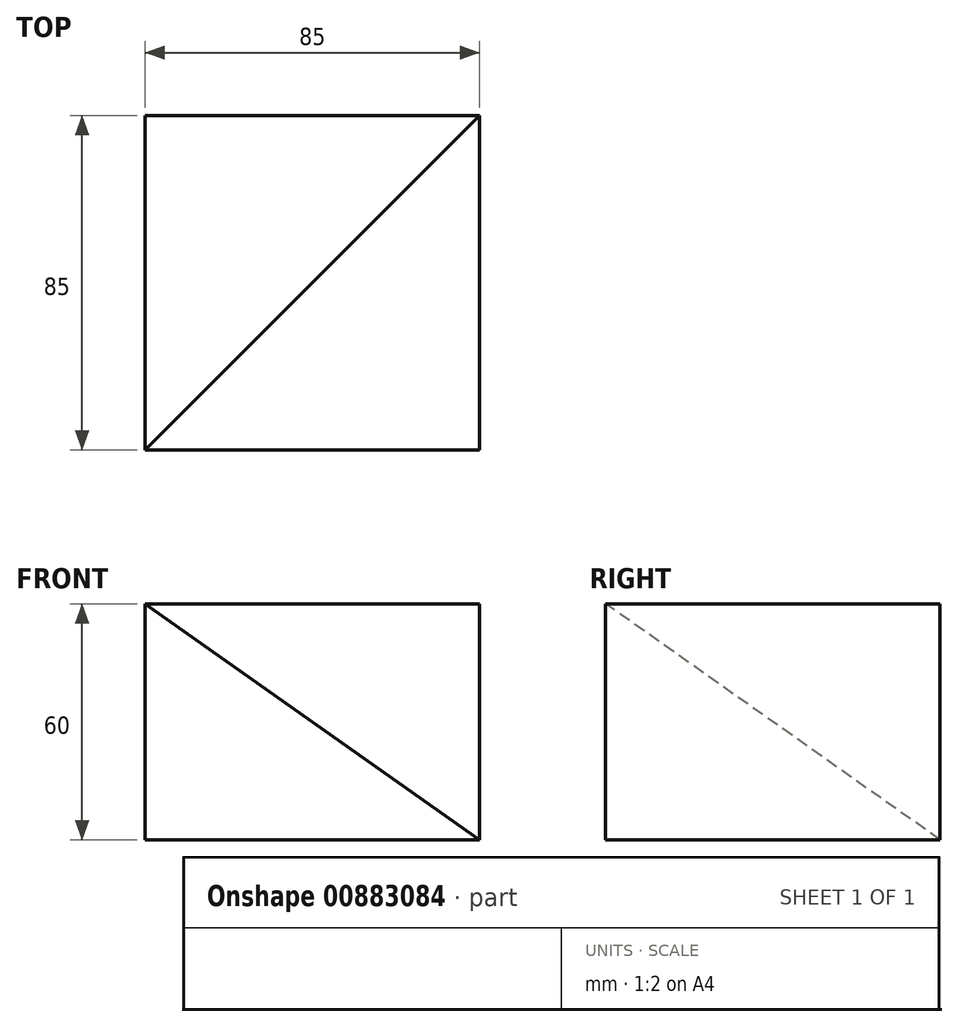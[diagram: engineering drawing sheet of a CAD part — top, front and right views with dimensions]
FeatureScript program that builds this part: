
annotation { "Feature Type Name" : "Feature", "Feature Type Description" : "" }
export const myFeature = defineFeature(function(context is Context, id is Id, definition is map)
    precondition{}
    {
        {
            var Q0;
            Q0=qCreatedBy(makeId("Top.planeOp"),FACE);
            var sketch = newSketch(context, id + "F0", { "sketchPlane" : qUnion([Q0])});
            skCircle(sketch, "E0.cCircle", {"center": v(0, 0) * mm, "radius": 42.5 * mm, "construction": true});
            skLineSegment(sketch, "E0.0", {"start": v(-42.5, 42.5) * mm, "end": v(42.5, 42.5) * mm});
            skLineSegment(sketch, "E0.1", {"start": v(42.5, 42.5) * mm, "end": v(42.5, -42.5) * mm});
            skLineSegment(sketch, "E0.2", {"start": v(42.5, -42.5) * mm, "end": v(-42.5, -42.5) * mm});
            skLineSegment(sketch, "E0.3", {"start": v(-42.5, -42.5) * mm, "end": v(-42.5, 42.5) * mm});
            skPoint(sketch, "E0.0.midPoint", {"position": v(0, 42.5) * mm});
            skSolve(sketch);
        }
        {
            var Q0;
            Q0=qCreatedBy(makeId("Top.planeOp"),FACE);
            cPlane(context, id + "F1", {"entities" : qUnion([Q0]), "cplaneType" : CPlaneType.OFFSET, "offset" : 60 * mm, "width" : 150 * mm, "height" : 150 * mm});
        }
        {
            var Q0;
            Q0=qCreatedBy(id+"F1.planeOp",FACE);
            var sketch = newSketch(context, id + "F2", { "sketchPlane" : qUnion([Q0])});
            skPoint(sketch, "E1", {"position": v(-42.5, -42.5) * mm});
            skSolve(sketch);
        }
        {
            var Q0;
            Q0=makeQuery(id+"F0.imprint","IMPRINT",FACE,{"disambiguationData":[TD([[makeQuery(id+"F0.imprint","IMPRINT",EDGE,{"derivedFrom":sQuery(id+"F0.wireOp",EDGE,"E0.0")}),-1.0]])]});
            var Q1;
            Q1=sQuery(id+"F2.wireOp",VERTEX,"E1");
            loft(context, id + "F3", {"sheetProfilesArray" : [{ "sheetProfileEntities" : qUnion([Q0]) }, { "sheetProfileEntities" : qUnion([Q1]) }]});
        }
        {
            var Q0;
            Q0=qCreatedBy(id+"F1.planeOp",FACE);
            var sketch = newSketch(context, id + "F4", { "sketchPlane" : qUnion([Q0])});
            skCircle(sketch, "E2.cCircle", {"center": v(0, 0) * mm, "radius": 42.5 * mm, "construction": true});
            skLineSegment(sketch, "E2.0", {"start": v(-42.5, 42.5) * mm, "end": v(42.5, 42.5) * mm});
            skLineSegment(sketch, "E2.1", {"start": v(42.5, 42.5) * mm, "end": v(42.5, -42.5) * mm});
            skLineSegment(sketch, "E2.2", {"start": v(42.5, -42.5) * mm, "end": v(-42.5, -42.5) * mm});
            skLineSegment(sketch, "E2.3", {"start": v(-42.5, -42.5) * mm, "end": v(-42.5, 42.5) * mm});
            skPoint(sketch, "E2.0.midPoint", {"position": v(0, 42.5) * mm});
            skLineSegment(sketch, "E3", {"start": v(42.5, 42.5) * mm, "end": v(-42.5, -42.5) * mm});
            skSolve(sketch);
        }
        {
            var Q1;
            Q1=makeQuery(id+"F4.imprint","IMPRINT",FACE,{"disambiguationData":[TD([[makeQuery(id+"F4.imprint","IMPRINT",EDGE,{"derivedFrom":sQuery(id+"F4.wireOp",EDGE,"E2.1")}),-1.0]])]});
            var Q2;
            Q2=makeQuery(id+"F3.opLoft","SWEPT_FACE",FACE,{"disambiguationData":[OSD([sQuery(id+"F0.wireOp",EDGE,"E0.0"),sQuery(id+"F0.wireOp",EDGE,"E0.1"),sQuery(id+"F0.wireOp",EDGE,"E0.2")])]});
            loft(context, id + "F5", {"sheetProfilesArray" : [{ "sheetProfileEntities" : qUnion([Q1]) }, { "sheetProfileEntities" : qUnion([Q2]) }]});
        }
        {
            var Q0;
            Q0=makeQuery(id+"F4.imprint","IMPRINT",FACE,{"disambiguationData":[TD([[makeQuery(id+"F4.imprint","IMPRINT",EDGE,{"derivedFrom":sQuery(id+"F4.wireOp",EDGE,"E2.0")}),-1.0]])]});
            var Q1;
            Q1=makeQuery(id+"F3.opLoft","SWEPT_FACE",FACE,{"disambiguationData":[OSD([sQuery(id+"F0.wireOp",EDGE,"E0.0"),sQuery(id+"F0.wireOp",EDGE,"E0.1"),sQuery(id+"F0.wireOp",EDGE,"E0.3")])]});
            loft(context, id + "F6", {"sheetProfilesArray" : [{ "sheetProfileEntities" : qUnion([Q0]) }, { "sheetProfileEntities" : qUnion([Q1]) }]});
        }
    });
